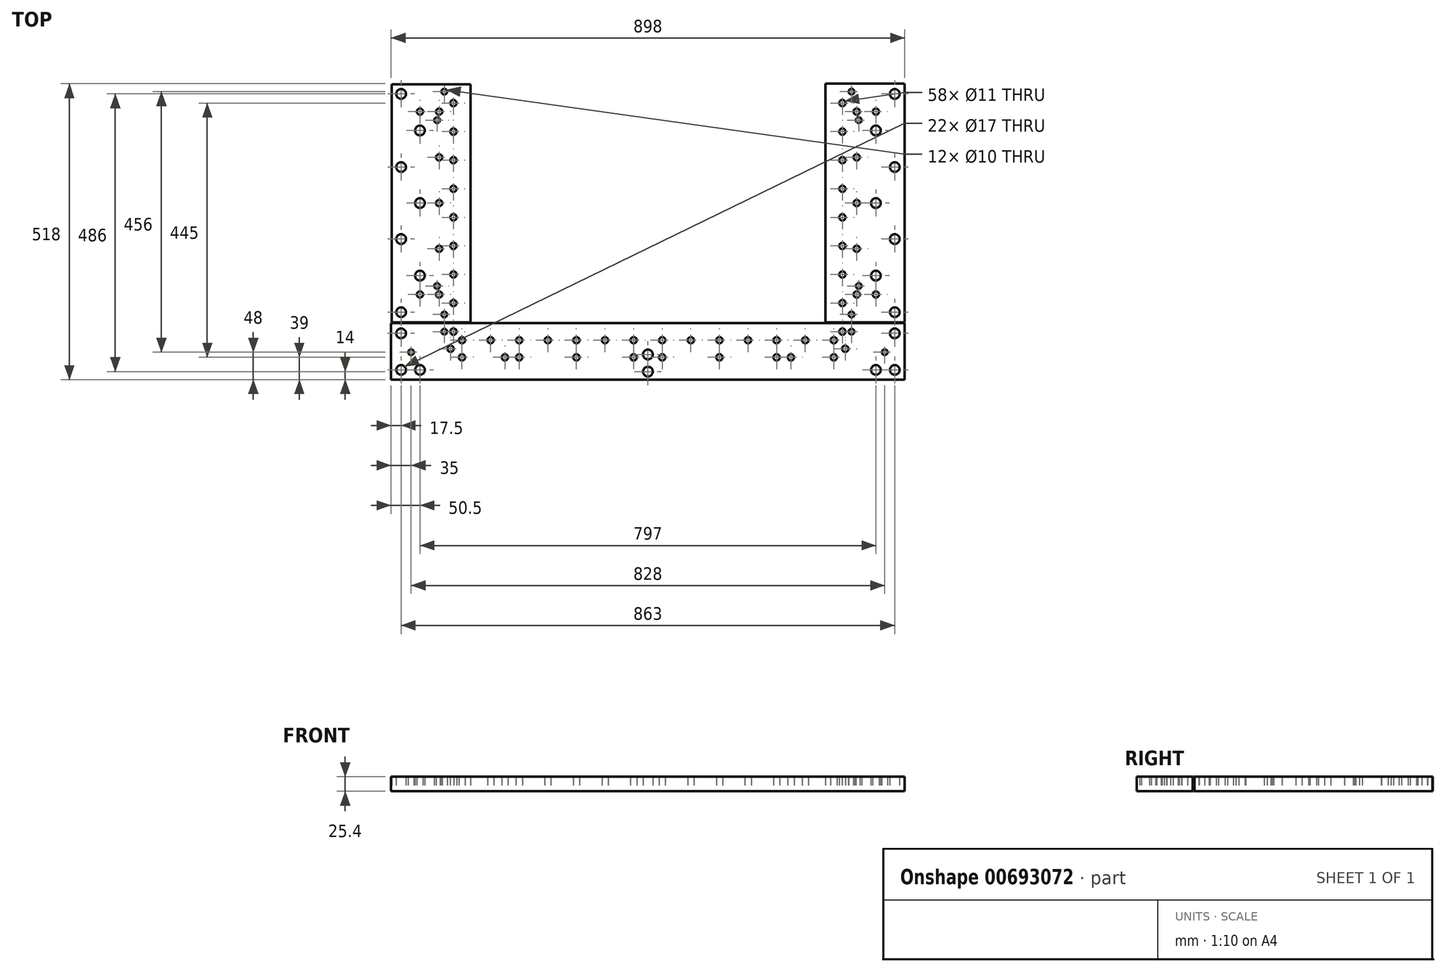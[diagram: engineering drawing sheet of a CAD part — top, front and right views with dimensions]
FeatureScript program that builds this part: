
annotation { "Feature Type Name" : "Feature", "Feature Type Description" : "" }
export const myFeature = defineFeature(function(context is Context, id is Id, definition is map)
    precondition{}
    {
        {
            var Q0;
            Q0=qCreatedBy(makeId("Top.planeOp"),FACE);
            var sketch = newSketch(context, id + "F0", { "sketchPlane" : qUnion([Q0])});
            skLineSegment(sketch, "E0", {"start": v(-449, 212.96) * mm, "end": v(-449, 208.04) * mm});
            skLineSegment(sketch, "E1", {"start": v(-449, 147.96) * mm, "end": v(-449, 143.04) * mm});
            skLineSegment(sketch, "E2", {"start": v(-449, 127.96) * mm, "end": v(-449, 123.04) * mm});
            skLineSegment(sketch, "E3", {"start": v(-449, 62.96) * mm, "end": v(-449, 58.04) * mm});
            skLineSegment(sketch, "E4", {"start": v(-449, 42.96) * mm, "end": v(-449, 38.04) * mm});
            skLineSegment(sketch, "E5", {"start": v(-449, -22.04) * mm, "end": v(-449, -26.96) * mm});
            skLineSegment(sketch, "E6", {"start": v(-449, -42.04) * mm, "end": v(-449, -46.96) * mm});
            skLineSegment(sketch, "E7", {"start": v(-449, 232.96) * mm, "end": v(-449, 228.04) * mm});
            skLineSegment(sketch, "E8", {"start": v(-449, -107.04) * mm, "end": v(-449, -111.96) * mm});
            skLineSegment(sketch, "E9", {"start": v(-449, -127.04) * mm, "end": v(-449, -131.96) * mm});
            skLineSegment(sketch, "E10", {"start": v(-339, 258.5) * mm, "end": v(-448, 258.5) * mm});
            skLineSegment(sketch, "E11", {"start": v(-448, 258.5) * mm, "end": v(-448, -157.5) * mm});
            skLineSegment(sketch, "E12", {"start": v(-339, 258.5) * mm, "end": v(-310, 258.5) * mm});
            skLineSegment(sketch, "E13", {"start": v(-310, 258.5) * mm, "end": v(-310, -157.5) * mm});
            skLineSegment(sketch, "E14", {"start": v(-339.41, 259.5) * mm, "end": v(-448, 259.5) * mm});
            skLineSegment(sketch, "E15", {"start": v(-448, 259.5) * mm, "end": v(-448.5, 259) * mm});
            skLineSegment(sketch, "E16", {"start": v(-448.5, 259) * mm, "end": v(-448, 258.5) * mm});
            skLineSegment(sketch, "E17", {"start": v(-339.41, 259.5) * mm, "end": v(-310, 259.5) * mm});
            skLineSegment(sketch, "E18", {"start": v(-310, 259.5) * mm, "end": v(-310, 258.5) * mm});
            skLineSegment(sketch, "E19", {"start": v(-448.5, 259) * mm, "end": v(-449, 258.5) * mm});
            skLineSegment(sketch, "E20", {"start": v(-449, 258.5) * mm, "end": v(-449, -157.5) * mm});
            skLineSegment(sketch, "E21", {"start": v(-449, -157.5) * mm, "end": v(-448.5, -158) * mm});
            skLineSegment(sketch, "E22", {"start": v(-448.5, -158) * mm, "end": v(-448, -157.5) * mm});
            skLineSegment(sketch, "E23", {"start": v(-448, 259.5) * mm, "end": v(-449, 258.5) * mm});
            skLineSegment(sketch, "E24", {"start": v(-310, -157.5) * mm, "end": v(-310, -158.5) * mm});
            skLineSegment(sketch, "E25", {"start": v(-310, -158.5) * mm, "end": v(-339.41, -158.5) * mm});
            skLineSegment(sketch, "E26", {"start": v(-448.5, -158) * mm, "end": v(-448, -158.5) * mm});
            skLineSegment(sketch, "E27", {"start": v(-448, -158.5) * mm, "end": v(-339.41, -158.5) * mm});
            skLineSegment(sketch, "E28", {"start": v(-449, -157.5) * mm, "end": v(-448, -158.5) * mm});
            skLineSegment(sketch, "E29", {"start": v(-310, -158.5) * mm, "end": v(-310, -158) * mm});
            skLineSegment(sketch, "E30", {"start": v(-310, -158) * mm, "end": v(-310, 259) * mm});
            skLineSegment(sketch, "E31", {"start": v(-310, 259) * mm, "end": v(-310, 259.5) * mm});
            skLineSegment(sketch, "E32", {"start": v(-310, 259.5) * mm, "end": v(-448, 259.5) * mm});
            skLineSegment(sketch, "E33", {"start": v(-449, 258.5) * mm, "end": v(-448, 258.5) * mm});
            skLineSegment(sketch, "E34", {"start": v(-448, 258.5) * mm, "end": v(-448, 259.5) * mm});
            skLineSegment(sketch, "E35", {"start": v(-448, -157.5) * mm, "end": v(-449, -157.5) * mm});
            skLineSegment(sketch, "E36", {"start": v(-448, -158.5) * mm, "end": v(-448, -157.5) * mm});
            skLineSegment(sketch, "E37", {"start": v(-448, -158.5) * mm, "end": v(-310, -158.5) * mm});
            skLineSegment(sketch, "E38", {"start": v(-310, 259) * mm, "end": v(-310.5, 258.5) * mm});
            skLineSegment(sketch, "E39", {"start": v(-448, 258.5) * mm, "end": v(-310.5, 258.5) * mm});
            skLineSegment(sketch, "E40", {"start": v(-448, -157.5) * mm, "end": v(-448, 258.5) * mm});
            skLineSegment(sketch, "E41", {"start": v(340, -119.5) * mm, "end": v(340, -119) * mm});
            skLineSegment(sketch, "E42", {"start": v(340, -130) * mm, "end": v(340, -129.5) * mm});
            skLineSegment(sketch, "E43", {"start": v(448, 258.5) * mm, "end": v(339, 258.5) * mm});
            skLineSegment(sketch, "E44", {"start": v(310, -157.5) * mm, "end": v(310, 258.5) * mm});
            skLineSegment(sketch, "E45", {"start": v(310, 258.5) * mm, "end": v(339, 258.5) * mm});
            skLineSegment(sketch, "E46", {"start": v(339.41, -158.5) * mm, "end": v(448, -158.5) * mm});
            skLineSegment(sketch, "E47", {"start": v(448, -158.5) * mm, "end": v(448.5, -158) * mm});
            skLineSegment(sketch, "E48", {"start": v(339.41, -158.5) * mm, "end": v(310, -158.5) * mm});
            skLineSegment(sketch, "E49", {"start": v(310, -158.5) * mm, "end": v(310, -157.5) * mm});
            skLineSegment(sketch, "E50", {"start": v(448.5, -158) * mm, "end": v(449, -157.5) * mm});
            skLineSegment(sketch, "E51", {"start": v(449, -157.5) * mm, "end": v(449, 258.5) * mm});
            skLineSegment(sketch, "E52", {"start": v(449, 258.5) * mm, "end": v(448.5, 259) * mm});
            skLineSegment(sketch, "E53", {"start": v(448, -158.5) * mm, "end": v(449, -157.5) * mm});
            skLineSegment(sketch, "E54", {"start": v(310, 258.5) * mm, "end": v(310, 259.5) * mm});
            skLineSegment(sketch, "E55", {"start": v(310, 259.5) * mm, "end": v(339.41, 259.5) * mm});
            skLineSegment(sketch, "E56", {"start": v(448.5, 259) * mm, "end": v(448, 259.5) * mm});
            skLineSegment(sketch, "E57", {"start": v(448, 259.5) * mm, "end": v(339.41, 259.5) * mm});
            skLineSegment(sketch, "E58", {"start": v(449, 258.5) * mm, "end": v(448, 259.5) * mm});
            skLineSegment(sketch, "E59", {"start": v(310, 259.5) * mm, "end": v(310, 259) * mm});
            skLineSegment(sketch, "E60", {"start": v(310, 259) * mm, "end": v(310, -158) * mm});
            skLineSegment(sketch, "E61", {"start": v(310, -158) * mm, "end": v(310, -158.5) * mm});
            skLineSegment(sketch, "E62", {"start": v(310, -158.5) * mm, "end": v(448, -158.5) * mm});
            skLineSegment(sketch, "E63", {"start": v(448, 259.5) * mm, "end": v(310, 259.5) * mm});
            skLineSegment(sketch, "E64", {"start": v(310.5, 258.5) * mm, "end": v(310, 259) * mm});
            skLineSegment(sketch, "E65", {"start": v(310.5, 258.5) * mm, "end": v(448, 258.5) * mm});
            skLineSegment(sketch, "E66", {"start": v(-382.46, -259.5) * mm, "end": v(-377.54, -259.5) * mm});
            skLineSegment(sketch, "E67", {"start": v(377.54, -259.5) * mm, "end": v(382.46, -259.5) * mm});
            skLineSegment(sketch, "E68", {"start": v(412.54, -259.5) * mm, "end": v(417.46, -259.5) * mm});
            skLineSegment(sketch, "E69", {"start": v(-417.46, -259.5) * mm, "end": v(-412.54, -259.5) * mm});
            skLineSegment(sketch, "E70", {"start": v(-65, -258.5) * mm, "end": v(-65, -259.5) * mm});
            skLineSegment(sketch, "E71", {"start": v(65, -259.5) * mm, "end": v(65, -258.5) * mm});
            skLineSegment(sketch, "E72", {"start": v(-65, -258.5) * mm, "end": v(-333, -258.5) * mm});
            skLineSegment(sketch, "E73", {"start": v(333, -258.5) * mm, "end": v(65, -258.5) * mm});
            skLineSegment(sketch, "E74", {"start": v(333, -258.5) * mm, "end": v(448, -258.5) * mm});
            skLineSegment(sketch, "E75", {"start": v(-448, -258.5) * mm, "end": v(-333, -258.5) * mm});
            skLineSegment(sketch, "E76", {"start": v(333, -258.5) * mm, "end": v(333, -259.5) * mm});
            skLineSegment(sketch, "E77", {"start": v(333, -259.5) * mm, "end": v(65, -259.5) * mm});
            skLineSegment(sketch, "E78", {"start": v(-65, -259.5) * mm, "end": v(65, -259.5) * mm});
            skLineSegment(sketch, "E79", {"start": v(-333, -259.5) * mm, "end": v(-333, -258.5) * mm});
            skLineSegment(sketch, "E80", {"start": v(-65, -259.5) * mm, "end": v(-333, -259.5) * mm});
            skLineSegment(sketch, "E81", {"start": v(-448, -258.5) * mm, "end": v(-448.5, -259) * mm});
            skLineSegment(sketch, "E82", {"start": v(-448.5, -259) * mm, "end": v(-448, -259.5) * mm});
            skLineSegment(sketch, "E83", {"start": v(-448, -259.5) * mm, "end": v(-333, -259.5) * mm});
            skLineSegment(sketch, "E84", {"start": v(333, -259.5) * mm, "end": v(448, -259.5) * mm});
            skLineSegment(sketch, "E85", {"start": v(448, -259.5) * mm, "end": v(448.5, -259) * mm});
            skLineSegment(sketch, "E86", {"start": v(448.5, -259) * mm, "end": v(448, -258.5) * mm});
            skLineSegment(sketch, "E87", {"start": v(448.5, -259) * mm, "end": v(449, -258.5) * mm});
            skLineSegment(sketch, "E88", {"start": v(449, -258.5) * mm, "end": v(449, -160.5) * mm});
            skLineSegment(sketch, "E89", {"start": v(449, -160.5) * mm, "end": v(448.5, -160) * mm});
            skLineSegment(sketch, "E90", {"start": v(448, -259.5) * mm, "end": v(449, -258.5) * mm});
            skLineSegment(sketch, "E91", {"start": v(-333, -159.5) * mm, "end": v(-448, -159.5) * mm});
            skLineSegment(sketch, "E92", {"start": v(-448, -159.5) * mm, "end": v(-448.5, -160) * mm});
            skLineSegment(sketch, "E93", {"start": v(-333, -159.5) * mm, "end": v(333, -159.5) * mm});
            skLineSegment(sketch, "E94", {"start": v(448.5, -160) * mm, "end": v(448, -159.5) * mm});
            skLineSegment(sketch, "E95", {"start": v(448, -159.5) * mm, "end": v(333, -159.5) * mm});
            skLineSegment(sketch, "E96", {"start": v(-448, -159.5) * mm, "end": v(-448.25, -159.75) * mm});
            skLineSegment(sketch, "E97", {"start": v(-448.25, -159.75) * mm, "end": v(-449, -160.5) * mm});
            skLineSegment(sketch, "E98", {"start": v(-449, -160.5) * mm, "end": v(-448.5, -160) * mm});
            skLineSegment(sketch, "E99", {"start": v(-448.5, -259) * mm, "end": v(-449, -258.5) * mm});
            skLineSegment(sketch, "E100", {"start": v(-449, -258.5) * mm, "end": v(-448, -259.5) * mm});
            skLineSegment(sketch, "E101", {"start": v(-449, -160.5) * mm, "end": v(-449, -258.5) * mm});
            skLineSegment(sketch, "E102", {"start": v(-448, -259.5) * mm, "end": v(448, -259.5) * mm});
            skLineSegment(sketch, "E103", {"start": v(449, -258.5) * mm, "end": v(448, -258.5) * mm});
            skLineSegment(sketch, "E104", {"start": v(448, -258.5) * mm, "end": v(448, -259.5) * mm});
            skLineSegment(sketch, "E105", {"start": v(448, -159.5) * mm, "end": v(-448, -159.5) * mm});
            skLineSegment(sketch, "E106", {"start": v(-448, -259.5) * mm, "end": v(-448, -258.5) * mm});
            skLineSegment(sketch, "E107", {"start": v(-448, -258.5) * mm, "end": v(-449, -258.5) * mm});
            skLineSegment(sketch, "E108", {"start": v(448, -258.5) * mm, "end": v(-448, -258.5) * mm});
            skLineSegment(sketch, "E109", {"start": v(-50, -259.5) * mm, "end": v(50, -259.5) * mm});
            skLineSegment(sketch, "E110", {"start": v(50, -259.5) * mm, "end": v(-50, -259.5) * mm});
            skArc(sketch, "E111", {"start": v(-431.5, -132) * mm, "mid": v(-440, -140.5) * mm, "end": v(-431.5, -149) * mm});
            skArc(sketch, "E112", {"start": v(-398.5, -68) * mm, "mid": v(-407, -76.5) * mm, "end": v(-398.5, -85) * mm});
            skArc(sketch, "E113", {"start": v(-431.5, -4) * mm, "mid": v(-440, -12.5) * mm, "end": v(-431.5, -21) * mm});
            skArc(sketch, "E114", {"start": v(-398.5, 59) * mm, "mid": v(-407, 50.5) * mm, "end": v(-398.5, 42) * mm});
            skArc(sketch, "E115", {"start": v(-431.5, 122) * mm, "mid": v(-440, 113.5) * mm, "end": v(-431.5, 105) * mm});
            skArc(sketch, "E116", {"start": v(-398.5, 186) * mm, "mid": v(-407, 177.5) * mm, "end": v(-398.5, 169) * mm});
            skArc(sketch, "E117", {"start": v(-431.5, 250) * mm, "mid": v(-440, 241.5) * mm, "end": v(-431.5, 233) * mm});
            skArc(sketch, "E118", {"start": v(-398.5, 216) * mm, "mid": v(-404, 210.5) * mm, "end": v(-398.5, 205) * mm});
            skArc(sketch, "E119", {"start": v(-365, 216) * mm, "mid": v(-370.5, 210.5) * mm, "end": v(-365, 205) * mm});
            skArc(sketch, "E120", {"start": v(-340, 231) * mm, "mid": v(-345.5, 225.5) * mm, "end": v(-340, 220) * mm});
            skArc(sketch, "E121", {"start": v(-340, 181) * mm, "mid": v(-345.5, 175.5) * mm, "end": v(-340, 170) * mm});
            skArc(sketch, "E122", {"start": v(-365, 136) * mm, "mid": v(-370.5, 130.5) * mm, "end": v(-365, 125) * mm});
            skArc(sketch, "E123", {"start": v(-340, 131) * mm, "mid": v(-345.5, 125.5) * mm, "end": v(-340, 120) * mm});
            skArc(sketch, "E124", {"start": v(-340, 81) * mm, "mid": v(-345.5, 75.5) * mm, "end": v(-340, 70) * mm});
            skArc(sketch, "E125", {"start": v(-365, 56) * mm, "mid": v(-370.5, 50.5) * mm, "end": v(-365, 45) * mm});
            skArc(sketch, "E126", {"start": v(-340, 31) * mm, "mid": v(-345.5, 25.5) * mm, "end": v(-340, 20) * mm});
            skArc(sketch, "E127", {"start": v(-340, -19) * mm, "mid": v(-345.5, -24.5) * mm, "end": v(-340, -30) * mm});
            skArc(sketch, "E128", {"start": v(-365, -24) * mm, "mid": v(-370.5, -29.5) * mm, "end": v(-365, -35) * mm});
            skArc(sketch, "E129", {"start": v(-340, -69) * mm, "mid": v(-345.5, -74.5) * mm, "end": v(-340, -80) * mm});
            skArc(sketch, "E130", {"start": v(-365, -104) * mm, "mid": v(-370.5, -109.5) * mm, "end": v(-365, -115) * mm});
            skArc(sketch, "E131", {"start": v(-340, -119) * mm, "mid": v(-345.5, -124.5) * mm, "end": v(-340, -130) * mm});
            skArc(sketch, "E132", {"start": v(-398.5, -104) * mm, "mid": v(-404, -109.5) * mm, "end": v(-398.5, -115) * mm});
            skArc(sketch, "E133", {"start": v(-356, -139.5) * mm, "mid": v(-361, -144.5) * mm, "end": v(-356, -149.5) * mm});
            skArc(sketch, "E134", {"start": v(-356, 250.5) * mm, "mid": v(-361, 245.5) * mm, "end": v(-356, 240.5) * mm});
            skArc(sketch, "E135", {"start": v(-368.5, 200.5) * mm, "mid": v(-373.5, 195.5) * mm, "end": v(-368.5, 190.5) * mm});
            skArc(sketch, "E136", {"start": v(-368.5, -89.5) * mm, "mid": v(-373.5, -94.5) * mm, "end": v(-368.5, -99.5) * mm});
            skArc(sketch, "E137", {"start": v(-368.5, -99.5) * mm, "mid": v(-363.5, -94.5) * mm, "end": v(-368.5, -89.5) * mm});
            skArc(sketch, "E138", {"start": v(-368.5, 190.5) * mm, "mid": v(-363.5, 195.5) * mm, "end": v(-368.5, 200.5) * mm});
            skArc(sketch, "E139", {"start": v(-356, 240.5) * mm, "mid": v(-351, 245.5) * mm, "end": v(-356, 250.5) * mm});
            skArc(sketch, "E140", {"start": v(-356, -149.5) * mm, "mid": v(-351, -144.5) * mm, "end": v(-356, -139.5) * mm});
            skArc(sketch, "E141", {"start": v(-398.5, -115) * mm, "mid": v(-393, -109.5) * mm, "end": v(-398.5, -104) * mm});
            skArc(sketch, "E142", {"start": v(-340, -130) * mm, "mid": v(-334.5, -124.5) * mm, "end": v(-340, -119) * mm});
            skArc(sketch, "E143", {"start": v(-365, -115) * mm, "mid": v(-359.5, -109.5) * mm, "end": v(-365, -104) * mm});
            skArc(sketch, "E144", {"start": v(-340, -80) * mm, "mid": v(-334.5, -74.5) * mm, "end": v(-340, -69) * mm});
            skArc(sketch, "E145", {"start": v(-365, -35) * mm, "mid": v(-359.5, -29.5) * mm, "end": v(-365, -24) * mm});
            skArc(sketch, "E146", {"start": v(-340, -30) * mm, "mid": v(-334.5, -24.5) * mm, "end": v(-340, -19) * mm});
            skArc(sketch, "E147", {"start": v(-340, 20) * mm, "mid": v(-334.5, 25.5) * mm, "end": v(-340, 31) * mm});
            skArc(sketch, "E148", {"start": v(-365, 45) * mm, "mid": v(-359.5, 50.5) * mm, "end": v(-365, 56) * mm});
            skArc(sketch, "E149", {"start": v(-340, 70) * mm, "mid": v(-334.5, 75.5) * mm, "end": v(-340, 81) * mm});
            skArc(sketch, "E150", {"start": v(-340, 120) * mm, "mid": v(-334.5, 125.5) * mm, "end": v(-340, 131) * mm});
            skArc(sketch, "E151", {"start": v(-365, 125) * mm, "mid": v(-359.5, 130.5) * mm, "end": v(-365, 136) * mm});
            skArc(sketch, "E152", {"start": v(-340, 170) * mm, "mid": v(-334.5, 175.5) * mm, "end": v(-340, 181) * mm});
            skArc(sketch, "E153", {"start": v(-340, 220) * mm, "mid": v(-334.5, 225.5) * mm, "end": v(-340, 231) * mm});
            skArc(sketch, "E154", {"start": v(-365, 205) * mm, "mid": v(-359.5, 210.5) * mm, "end": v(-365, 216) * mm});
            skArc(sketch, "E155", {"start": v(-398.5, 205) * mm, "mid": v(-393, 210.5) * mm, "end": v(-398.5, 216) * mm});
            skArc(sketch, "E156", {"start": v(-431.5, 233) * mm, "mid": v(-423, 241.5) * mm, "end": v(-431.5, 250) * mm});
            skArc(sketch, "E157", {"start": v(-398.5, 169) * mm, "mid": v(-390, 177.5) * mm, "end": v(-398.5, 186) * mm});
            skArc(sketch, "E158", {"start": v(-431.5, 105) * mm, "mid": v(-423, 113.5) * mm, "end": v(-431.5, 122) * mm});
            skArc(sketch, "E159", {"start": v(-398.5, 42) * mm, "mid": v(-390, 50.5) * mm, "end": v(-398.5, 59) * mm});
            skArc(sketch, "E160", {"start": v(-431.5, -21) * mm, "mid": v(-423, -12.5) * mm, "end": v(-431.5, -4) * mm});
            skArc(sketch, "E161", {"start": v(-398.5, -85) * mm, "mid": v(-390, -76.5) * mm, "end": v(-398.5, -68) * mm});
            skArc(sketch, "E162", {"start": v(-431.5, -149) * mm, "mid": v(-423, -140.5) * mm, "end": v(-431.5, -132) * mm});
            skArc(sketch, "E163", {"start": v(431.5, 233) * mm, "mid": v(440, 241.5) * mm, "end": v(431.5, 250) * mm});
            skArc(sketch, "E164", {"start": v(398.5, 169) * mm, "mid": v(407, 177.5) * mm, "end": v(398.5, 186) * mm});
            skArc(sketch, "E165", {"start": v(431.5, 105) * mm, "mid": v(440, 113.5) * mm, "end": v(431.5, 122) * mm});
            skArc(sketch, "E166", {"start": v(398.5, 42) * mm, "mid": v(407, 50.5) * mm, "end": v(398.5, 59) * mm});
            skArc(sketch, "E167", {"start": v(431.5, -21) * mm, "mid": v(440, -12.5) * mm, "end": v(431.5, -4) * mm});
            skArc(sketch, "E168", {"start": v(398.5, -85) * mm, "mid": v(407, -76.5) * mm, "end": v(398.5, -68) * mm});
            skArc(sketch, "E169", {"start": v(431.5, -149) * mm, "mid": v(440, -140.5) * mm, "end": v(431.5, -132) * mm});
            skArc(sketch, "E170", {"start": v(398.5, -115) * mm, "mid": v(404, -109.5) * mm, "end": v(398.5, -104) * mm});
            skArc(sketch, "E171", {"start": v(365, -115) * mm, "mid": v(370.5, -109.5) * mm, "end": v(365, -104) * mm});
            skArc(sketch, "E172", {"start": v(340, -130) * mm, "mid": v(345.5, -124.5) * mm, "end": v(340, -119) * mm});
            skArc(sketch, "E173", {"start": v(340, -80) * mm, "mid": v(345.5, -74.5) * mm, "end": v(340, -69) * mm});
            skArc(sketch, "E174", {"start": v(365, -35) * mm, "mid": v(370.5, -29.5) * mm, "end": v(365, -24) * mm});
            skArc(sketch, "E175", {"start": v(340, -30) * mm, "mid": v(345.5, -24.5) * mm, "end": v(340, -19) * mm});
            skArc(sketch, "E176", {"start": v(340, 20) * mm, "mid": v(345.5, 25.5) * mm, "end": v(340, 31) * mm});
            skArc(sketch, "E177", {"start": v(365, 45) * mm, "mid": v(370.5, 50.5) * mm, "end": v(365, 56) * mm});
            skArc(sketch, "E178", {"start": v(340, 70) * mm, "mid": v(345.5, 75.5) * mm, "end": v(340, 81) * mm});
            skArc(sketch, "E179", {"start": v(340, 120) * mm, "mid": v(345.5, 125.5) * mm, "end": v(340, 131) * mm});
            skArc(sketch, "E180", {"start": v(365, 125) * mm, "mid": v(370.5, 130.5) * mm, "end": v(365, 136) * mm});
            skArc(sketch, "E181", {"start": v(340, 170) * mm, "mid": v(345.5, 175.5) * mm, "end": v(340, 181) * mm});
            skArc(sketch, "E182", {"start": v(365, 205) * mm, "mid": v(370.5, 210.5) * mm, "end": v(365, 216) * mm});
            skArc(sketch, "E183", {"start": v(340, 220) * mm, "mid": v(345.5, 225.5) * mm, "end": v(340, 231) * mm});
            skArc(sketch, "E184", {"start": v(398.5, 205) * mm, "mid": v(404, 210.5) * mm, "end": v(398.5, 216) * mm});
            skArc(sketch, "E185", {"start": v(356, 240.5) * mm, "mid": v(361, 245.5) * mm, "end": v(356, 250.5) * mm});
            skArc(sketch, "E186", {"start": v(356, -149.5) * mm, "mid": v(361, -144.5) * mm, "end": v(356, -139.5) * mm});
            skArc(sketch, "E187", {"start": v(368.5, -99.5) * mm, "mid": v(373.5, -94.5) * mm, "end": v(368.5, -89.5) * mm});
            skArc(sketch, "E188", {"start": v(368.5, 190.5) * mm, "mid": v(373.5, 195.5) * mm, "end": v(368.5, 200.5) * mm});
            skArc(sketch, "E189", {"start": v(368.5, 200.5) * mm, "mid": v(363.5, 195.5) * mm, "end": v(368.5, 190.5) * mm});
            skArc(sketch, "E190", {"start": v(368.5, -89.5) * mm, "mid": v(363.5, -94.5) * mm, "end": v(368.5, -99.5) * mm});
            skArc(sketch, "E191", {"start": v(356, -139.5) * mm, "mid": v(351, -144.5) * mm, "end": v(356, -149.5) * mm});
            skArc(sketch, "E192", {"start": v(356, 250.5) * mm, "mid": v(351, 245.5) * mm, "end": v(356, 240.5) * mm});
            skArc(sketch, "E193", {"start": v(398.5, 216) * mm, "mid": v(393, 210.5) * mm, "end": v(398.5, 205) * mm});
            skArc(sketch, "E194", {"start": v(340, 231) * mm, "mid": v(334.5, 225.5) * mm, "end": v(340, 220) * mm});
            skArc(sketch, "E195", {"start": v(365, 216) * mm, "mid": v(359.5, 210.5) * mm, "end": v(365, 205) * mm});
            skArc(sketch, "E196", {"start": v(340, 181) * mm, "mid": v(334.5, 175.5) * mm, "end": v(340, 170) * mm});
            skArc(sketch, "E197", {"start": v(365, 136) * mm, "mid": v(359.5, 130.5) * mm, "end": v(365, 125) * mm});
            skArc(sketch, "E198", {"start": v(340, 131) * mm, "mid": v(334.5, 125.5) * mm, "end": v(340, 120) * mm});
            skArc(sketch, "E199", {"start": v(340, 81) * mm, "mid": v(334.5, 75.5) * mm, "end": v(340, 70) * mm});
            skArc(sketch, "E200", {"start": v(365, 56) * mm, "mid": v(359.5, 50.5) * mm, "end": v(365, 45) * mm});
            skArc(sketch, "E201", {"start": v(340, 31) * mm, "mid": v(334.5, 25.5) * mm, "end": v(340, 20) * mm});
            skArc(sketch, "E202", {"start": v(340, -19) * mm, "mid": v(334.5, -24.5) * mm, "end": v(340, -30) * mm});
            skArc(sketch, "E203", {"start": v(365, -24) * mm, "mid": v(359.5, -29.5) * mm, "end": v(365, -35) * mm});
            skArc(sketch, "E204", {"start": v(340, -69) * mm, "mid": v(334.5, -74.5) * mm, "end": v(340, -80) * mm});
            skArc(sketch, "E205", {"start": v(340, -119) * mm, "mid": v(334.5, -124.5) * mm, "end": v(340, -130) * mm});
            skArc(sketch, "E206", {"start": v(365, -104) * mm, "mid": v(359.5, -109.5) * mm, "end": v(365, -115) * mm});
            skArc(sketch, "E207", {"start": v(398.5, -104) * mm, "mid": v(393, -109.5) * mm, "end": v(398.5, -115) * mm});
            skArc(sketch, "E208", {"start": v(431.5, -132) * mm, "mid": v(423, -140.5) * mm, "end": v(431.5, -149) * mm});
            skArc(sketch, "E209", {"start": v(398.5, -68) * mm, "mid": v(390, -76.5) * mm, "end": v(398.5, -85) * mm});
            skArc(sketch, "E210", {"start": v(431.5, -4) * mm, "mid": v(423, -12.5) * mm, "end": v(431.5, -21) * mm});
            skArc(sketch, "E211", {"start": v(398.5, 59) * mm, "mid": v(390, 50.5) * mm, "end": v(398.5, 42) * mm});
            skArc(sketch, "E212", {"start": v(431.5, 122) * mm, "mid": v(423, 113.5) * mm, "end": v(431.5, 105) * mm});
            skArc(sketch, "E213", {"start": v(398.5, 186) * mm, "mid": v(390, 177.5) * mm, "end": v(398.5, 169) * mm});
            skArc(sketch, "E214", {"start": v(431.5, 250) * mm, "mid": v(423, 241.5) * mm, "end": v(431.5, 233) * mm});
            skArc(sketch, "E215", {"start": v(-440, -177.5) * mm, "mid": v(-431.5, -186) * mm, "end": v(-423, -177.5) * mm});
            skArc(sketch, "E216", {"start": v(-440, -241.5) * mm, "mid": v(-431.5, -250) * mm, "end": v(-423, -241.5) * mm});
            skArc(sketch, "E217", {"start": v(-407, -241.5) * mm, "mid": v(-398.5, -250) * mm, "end": v(-390, -241.5) * mm});
            skArc(sketch, "E218", {"start": v(-8.5, -214.5) * mm, "mid": v(0, -223) * mm, "end": v(8.5, -214.5) * mm});
            skArc(sketch, "E219", {"start": v(-8.5, -244.5) * mm, "mid": v(0, -253) * mm, "end": v(8.5, -244.5) * mm});
            skArc(sketch, "E220", {"start": v(390, -241.5) * mm, "mid": v(398.5, -250) * mm, "end": v(407, -241.5) * mm});
            skArc(sketch, "E221", {"start": v(423, -241.5) * mm, "mid": v(431.5, -250) * mm, "end": v(440, -241.5) * mm});
            skArc(sketch, "E222", {"start": v(423, -177.5) * mm, "mid": v(431.5, -186) * mm, "end": v(440, -177.5) * mm});
            skArc(sketch, "E223", {"start": v(-350.5, -204.5) * mm, "mid": v(-345, -210) * mm, "end": v(-339.5, -204.5) * mm});
            skArc(sketch, "E224", {"start": v(-345.5, -174.5) * mm, "mid": v(-340, -180) * mm, "end": v(-334.5, -174.5) * mm});
            skArc(sketch, "E225", {"start": v(-330.5, -189.5) * mm, "mid": v(-325, -195) * mm, "end": v(-319.5, -189.5) * mm});
            skArc(sketch, "E226", {"start": v(-330.5, -219.5) * mm, "mid": v(-325, -225) * mm, "end": v(-319.5, -219.5) * mm});
            skArc(sketch, "E227", {"start": v(-280.5, -189.5) * mm, "mid": v(-275, -195) * mm, "end": v(-269.5, -189.5) * mm});
            skArc(sketch, "E228", {"start": v(-255.5, -219.5) * mm, "mid": v(-250, -225) * mm, "end": v(-244.5, -219.5) * mm});
            skArc(sketch, "E229", {"start": v(-230.5, -219.5) * mm, "mid": v(-225, -225) * mm, "end": v(-219.5, -219.5) * mm});
            skArc(sketch, "E230", {"start": v(-230.5, -189.5) * mm, "mid": v(-225, -195) * mm, "end": v(-219.5, -189.5) * mm});
            skArc(sketch, "E231", {"start": v(-180.5, -189.5) * mm, "mid": v(-175, -195) * mm, "end": v(-169.5, -189.5) * mm});
            skArc(sketch, "E232", {"start": v(-130.5, -189.5) * mm, "mid": v(-125, -195) * mm, "end": v(-119.5, -189.5) * mm});
            skArc(sketch, "E233", {"start": v(-130.5, -219.5) * mm, "mid": v(-125, -225) * mm, "end": v(-119.5, -219.5) * mm});
            skArc(sketch, "E234", {"start": v(-80.5, -189.5) * mm, "mid": v(-75, -195) * mm, "end": v(-69.5, -189.5) * mm});
            skArc(sketch, "E235", {"start": v(-30.5, -219.5) * mm, "mid": v(-25, -225) * mm, "end": v(-19.5, -219.5) * mm});
            skArc(sketch, "E236", {"start": v(-30.5, -189.5) * mm, "mid": v(-25, -195) * mm, "end": v(-19.5, -189.5) * mm});
            skArc(sketch, "E237", {"start": v(19.5, -189.5) * mm, "mid": v(25, -195) * mm, "end": v(30.5, -189.5) * mm});
            skArc(sketch, "E238", {"start": v(19.5, -219.5) * mm, "mid": v(25, -225) * mm, "end": v(30.5, -219.5) * mm});
            skArc(sketch, "E239", {"start": v(69.5, -189.5) * mm, "mid": v(75, -195) * mm, "end": v(80.5, -189.5) * mm});
            skArc(sketch, "E240", {"start": v(119.5, -189.5) * mm, "mid": v(125, -195) * mm, "end": v(130.5, -189.5) * mm});
            skArc(sketch, "E241", {"start": v(119.5, -219.5) * mm, "mid": v(125, -225) * mm, "end": v(130.5, -219.5) * mm});
            skArc(sketch, "E242", {"start": v(169.5, -189.5) * mm, "mid": v(175, -195) * mm, "end": v(180.5, -189.5) * mm});
            skArc(sketch, "E243", {"start": v(219.5, -189.5) * mm, "mid": v(225, -195) * mm, "end": v(230.5, -189.5) * mm});
            skArc(sketch, "E244", {"start": v(219.5, -219.5) * mm, "mid": v(225, -225) * mm, "end": v(230.5, -219.5) * mm});
            skArc(sketch, "E245", {"start": v(244.5, -219.5) * mm, "mid": v(250, -225) * mm, "end": v(255.5, -219.5) * mm});
            skArc(sketch, "E246", {"start": v(269.5, -189.5) * mm, "mid": v(275, -195) * mm, "end": v(280.5, -189.5) * mm});
            skArc(sketch, "E247", {"start": v(319.5, -189.5) * mm, "mid": v(325, -195) * mm, "end": v(330.5, -189.5) * mm});
            skArc(sketch, "E248", {"start": v(334.5, -174.5) * mm, "mid": v(340, -180) * mm, "end": v(345.5, -174.5) * mm});
            skArc(sketch, "E249", {"start": v(339.5, -204.5) * mm, "mid": v(345, -210) * mm, "end": v(350.5, -204.5) * mm});
            skArc(sketch, "E250", {"start": v(319.5, -219.5) * mm, "mid": v(325, -225) * mm, "end": v(330.5, -219.5) * mm});
            skArc(sketch, "E251", {"start": v(-419, -210.5) * mm, "mid": v(-414, -215.5) * mm, "end": v(-409, -210.5) * mm});
            skArc(sketch, "E252", {"start": v(-361, -174.5) * mm, "mid": v(-356, -179.5) * mm, "end": v(-351, -174.5) * mm});
            skArc(sketch, "E253", {"start": v(409, -210.5) * mm, "mid": v(414, -215.5) * mm, "end": v(419, -210.5) * mm});
            skArc(sketch, "E254", {"start": v(351, -174.5) * mm, "mid": v(356, -179.5) * mm, "end": v(361, -174.5) * mm});
            skArc(sketch, "E255", {"start": v(361, -174.5) * mm, "mid": v(356, -169.5) * mm, "end": v(351, -174.5) * mm});
            skArc(sketch, "E256", {"start": v(419, -210.5) * mm, "mid": v(414, -205.5) * mm, "end": v(409, -210.5) * mm});
            skArc(sketch, "E257", {"start": v(-351, -174.5) * mm, "mid": v(-356, -169.5) * mm, "end": v(-361, -174.5) * mm});
            skArc(sketch, "E258", {"start": v(-409, -210.5) * mm, "mid": v(-414, -205.5) * mm, "end": v(-419, -210.5) * mm});
            skArc(sketch, "E259", {"start": v(330.5, -219.5) * mm, "mid": v(325, -214) * mm, "end": v(319.5, -219.5) * mm});
            skArc(sketch, "E260", {"start": v(350.5, -204.5) * mm, "mid": v(345, -199) * mm, "end": v(339.5, -204.5) * mm});
            skArc(sketch, "E261", {"start": v(345.5, -174.5) * mm, "mid": v(340, -169) * mm, "end": v(334.5, -174.5) * mm});
            skArc(sketch, "E262", {"start": v(330.5, -189.5) * mm, "mid": v(325, -184) * mm, "end": v(319.5, -189.5) * mm});
            skArc(sketch, "E263", {"start": v(280.5, -189.5) * mm, "mid": v(275, -184) * mm, "end": v(269.5, -189.5) * mm});
            skArc(sketch, "E264", {"start": v(255.5, -219.5) * mm, "mid": v(250, -214) * mm, "end": v(244.5, -219.5) * mm});
            skArc(sketch, "E265", {"start": v(230.5, -219.5) * mm, "mid": v(225, -214) * mm, "end": v(219.5, -219.5) * mm});
            skArc(sketch, "E266", {"start": v(230.5, -189.5) * mm, "mid": v(225, -184) * mm, "end": v(219.5, -189.5) * mm});
            skArc(sketch, "E267", {"start": v(180.5, -189.5) * mm, "mid": v(175, -184) * mm, "end": v(169.5, -189.5) * mm});
            skArc(sketch, "E268", {"start": v(130.5, -219.5) * mm, "mid": v(125, -214) * mm, "end": v(119.5, -219.5) * mm});
            skArc(sketch, "E269", {"start": v(130.5, -189.5) * mm, "mid": v(125, -184) * mm, "end": v(119.5, -189.5) * mm});
            skArc(sketch, "E270", {"start": v(80.5, -189.5) * mm, "mid": v(75, -184) * mm, "end": v(69.5, -189.5) * mm});
            skArc(sketch, "E271", {"start": v(30.5, -219.5) * mm, "mid": v(25, -214) * mm, "end": v(19.5, -219.5) * mm});
            skArc(sketch, "E272", {"start": v(30.5, -189.5) * mm, "mid": v(25, -184) * mm, "end": v(19.5, -189.5) * mm});
            skArc(sketch, "E273", {"start": v(-19.5, -189.5) * mm, "mid": v(-25, -184) * mm, "end": v(-30.5, -189.5) * mm});
            skArc(sketch, "E274", {"start": v(-19.5, -219.5) * mm, "mid": v(-25, -214) * mm, "end": v(-30.5, -219.5) * mm});
            skArc(sketch, "E275", {"start": v(-69.5, -189.5) * mm, "mid": v(-75, -184) * mm, "end": v(-80.5, -189.5) * mm});
            skArc(sketch, "E276", {"start": v(-119.5, -219.5) * mm, "mid": v(-125, -214) * mm, "end": v(-130.5, -219.5) * mm});
            skArc(sketch, "E277", {"start": v(-119.5, -189.5) * mm, "mid": v(-125, -184) * mm, "end": v(-130.5, -189.5) * mm});
            skArc(sketch, "E278", {"start": v(-169.5, -189.5) * mm, "mid": v(-175, -184) * mm, "end": v(-180.5, -189.5) * mm});
            skArc(sketch, "E279", {"start": v(-219.5, -189.5) * mm, "mid": v(-225, -184) * mm, "end": v(-230.5, -189.5) * mm});
            skArc(sketch, "E280", {"start": v(-219.5, -219.5) * mm, "mid": v(-225, -214) * mm, "end": v(-230.5, -219.5) * mm});
            skArc(sketch, "E281", {"start": v(-244.5, -219.5) * mm, "mid": v(-250, -214) * mm, "end": v(-255.5, -219.5) * mm});
            skArc(sketch, "E282", {"start": v(-269.5, -189.5) * mm, "mid": v(-275, -184) * mm, "end": v(-280.5, -189.5) * mm});
            skArc(sketch, "E283", {"start": v(-319.5, -219.5) * mm, "mid": v(-325, -214) * mm, "end": v(-330.5, -219.5) * mm});
            skArc(sketch, "E284", {"start": v(-319.5, -189.5) * mm, "mid": v(-325, -184) * mm, "end": v(-330.5, -189.5) * mm});
            skArc(sketch, "E285", {"start": v(-334.5, -174.5) * mm, "mid": v(-340, -169) * mm, "end": v(-345.5, -174.5) * mm});
            skArc(sketch, "E286", {"start": v(-339.5, -204.5) * mm, "mid": v(-345, -199) * mm, "end": v(-350.5, -204.5) * mm});
            skArc(sketch, "E287", {"start": v(440, -177.5) * mm, "mid": v(431.5, -169) * mm, "end": v(423, -177.5) * mm});
            skArc(sketch, "E288", {"start": v(440, -241.5) * mm, "mid": v(431.5, -233) * mm, "end": v(423, -241.5) * mm});
            skArc(sketch, "E289", {"start": v(407, -241.5) * mm, "mid": v(398.5, -233) * mm, "end": v(390, -241.5) * mm});
            skArc(sketch, "E290", {"start": v(8.5, -244.5) * mm, "mid": v(0, -236) * mm, "end": v(-8.5, -244.5) * mm});
            skArc(sketch, "E291", {"start": v(8.5, -214.5) * mm, "mid": v(0, -206) * mm, "end": v(-8.5, -214.5) * mm});
            skArc(sketch, "E292", {"start": v(-390, -241.5) * mm, "mid": v(-398.5, -233) * mm, "end": v(-407, -241.5) * mm});
            skArc(sketch, "E293", {"start": v(-423, -241.5) * mm, "mid": v(-431.5, -233) * mm, "end": v(-440, -241.5) * mm});
            skArc(sketch, "E294", {"start": v(-423, -177.5) * mm, "mid": v(-431.5, -169) * mm, "end": v(-440, -177.5) * mm});
            skSolve(sketch);
        }
        {
            var Q0;
            {var subQ0=sQuery(id+"F0.wireOp",EDGE,"E12");Q0=makeQuery(id+"F0.imprint","IMPRINT",FACE,{"disambiguationData":[TD([[makeQuery(id+"F0.imprint","IMPRINT",EDGE,{"derivedFrom":subQ0}),-1.0]])]});}
            var Q1;
            Q1=makeQuery(id+"F0.imprint","IMPRINT",FACE,{"disambiguationData":[TD([[makeQuery(id+"F0.imprint","IMPRINT",EDGE,{"derivedFrom":sQuery(id+"F0.wireOp",EDGE,"E89")}),1.0]])]});
            var Q2;
            {var subQ2=sQuery(id+"F0.wireOp",EDGE,"E45");Q2=makeQuery(id+"F0.imprint","IMPRINT",FACE,{"disambiguationData":[TD([[makeQuery(id+"F0.imprint","IMPRINT",EDGE,{"derivedFrom":subQ2}),-1.0]])]});}
            extrude(context, id + "F1", {"entities" : qUnion([Q0, Q1, Q2]), "depth" : 25.4 * mm, "offsetDistance" : 25.4 * mm});
        }
    });
